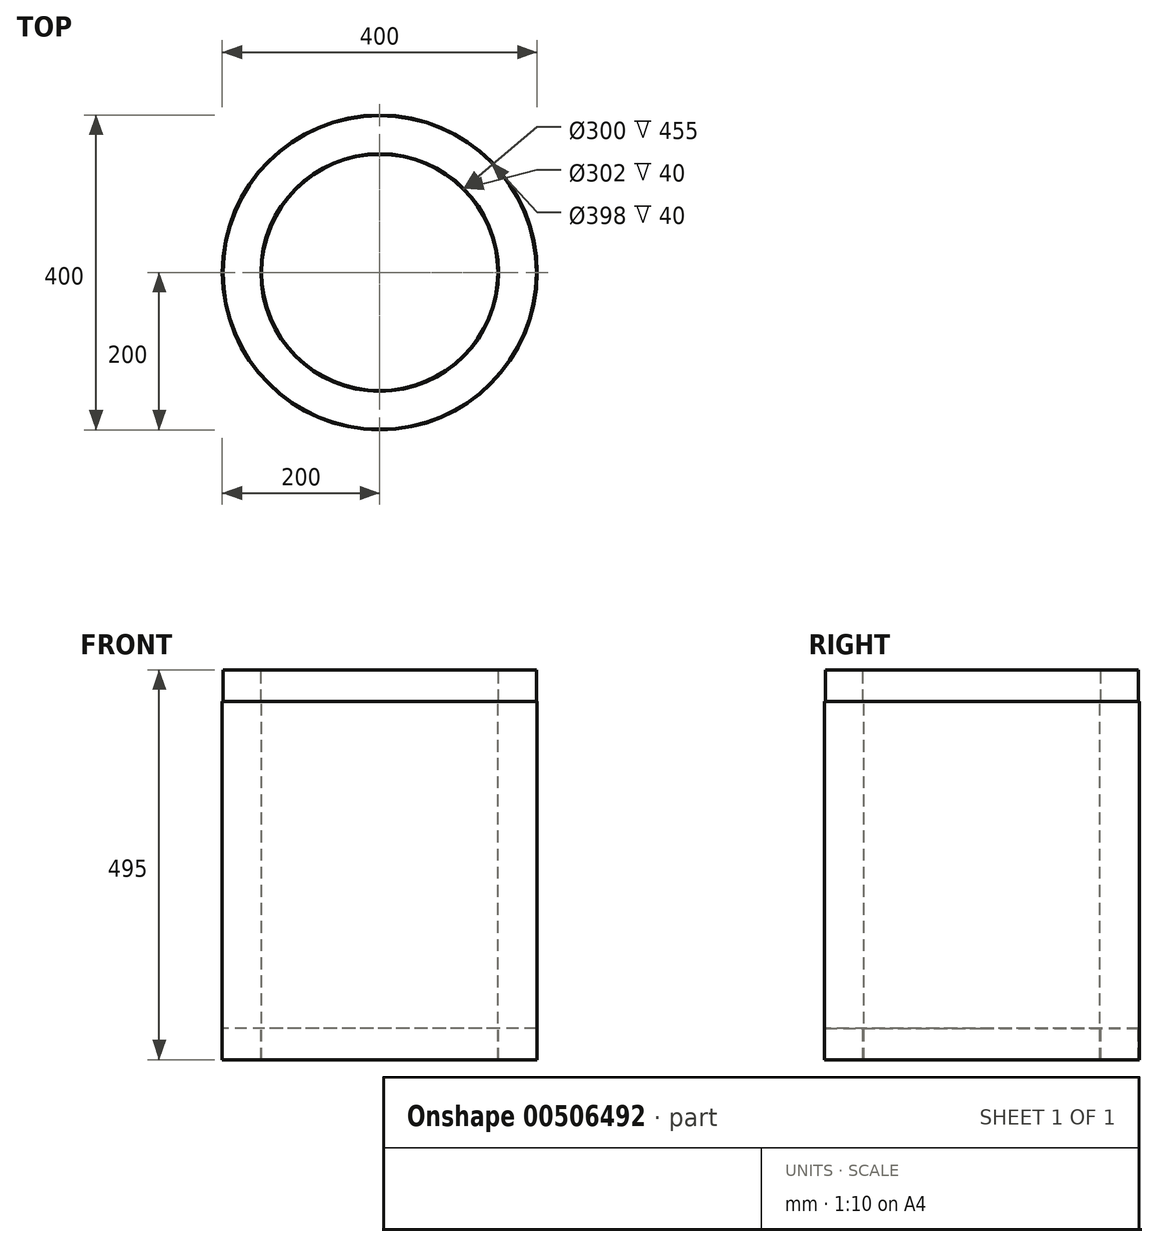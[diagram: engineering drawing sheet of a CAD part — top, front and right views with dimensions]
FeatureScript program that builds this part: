
annotation { "Feature Type Name" : "Feature", "Feature Type Description" : "" }
export const myFeature = defineFeature(function(context is Context, id is Id, definition is map)
    precondition{}
    {
        {
            var Q0;
            Q0=qCreatedBy(makeId("Front.planeOp"),FACE);
            var sketch = newSketch(context, id + "F0", { "sketchPlane" : qUnion([Q0])});
            skLineSegment(sketch, "E0", {"start": v(0, 74.87) * mm, "end": v(0, -73.71) * mm, "construction": true});
            skLineSegment(sketch, "E1", {"start": v(0, 374.84) * mm, "end": v(0, -528.94) * mm, "construction": true});
            skLineSegment(sketch, "E2", {"start": v(-150, -489.75) * mm, "end": v(-150, -34.75) * mm});
            skLineSegment(sketch, "E3", {"start": v(-150, -34.75) * mm, "end": v(-151, -34.75) * mm});
            skLineSegment(sketch, "E4", {"start": v(-151, -34.75) * mm, "end": v(-151, 5.25) * mm});
            skLineSegment(sketch, "E5", {"start": v(-151, 5.25) * mm, "end": v(-199, 5.25) * mm});
            skLineSegment(sketch, "E6", {"start": v(-199, 5.25) * mm, "end": v(-199, -34.75) * mm});
            skLineSegment(sketch, "E7", {"start": v(-199, -34.75) * mm, "end": v(-200, -34.75) * mm});
            skLineSegment(sketch, "E8", {"start": v(-200, -34.75) * mm, "end": v(-200, -489.75) * mm});
            skLineSegment(sketch, "E9", {"start": v(-200, -489.75) * mm, "end": v(-199, -489.75) * mm});
            skLineSegment(sketch, "E10", {"start": v(-199, -489.75) * mm, "end": v(-199, -449.75) * mm});
            skLineSegment(sketch, "E11", {"start": v(-199, -449.75) * mm, "end": v(-151, -449.75) * mm});
            skLineSegment(sketch, "E12", {"start": v(-151, -449.75) * mm, "end": v(-151, -489.75) * mm});
            skLineSegment(sketch, "E13", {"start": v(-151, -489.75) * mm, "end": v(-150, -489.75) * mm});
            skSolve(sketch);
        }
        {
            var Q0;
            Q0=qSketchRegion(id+"F0",true);
            var Q1;
            Q1=sQuery(id+"F0.wireOp",EDGE,"E1");
            revolve(context, id + "F1", {"entities" : qUnion([Q0]), "axis" : qUnion([Q1]), "revolveType" : RevolveType.FULL});
        }
    });
